# Revit family: Facade smoke exhaust hatch mcr_LAM
name_source: partatom
category: Okna
revit_build: Autodesk Revit 2018 (Build: 20170927_1515(x64)
units: mm (PartAtom-declared; Revit-internal decimal feet)

## family parameters
Obiekt nadrzędny = Powierzchnia
Punkt obliczania pomieszczeń = Nie
Tnij formami wycięć po wczytaniu = Nie
Współdzielony = Nie

## types (199) — shared parameters
Attention = You can choose steel or aluminum for the damper base
DBD = 148 mm
Model = mcr LAM
Opis = "Facade natural smoke and heat exhaust ventilator, louvered type mcr LAM"
Producent = Mercor S.A.
SBD = 150 mm
URL = https://www.mercor.com.pl
mcr_Acces space = mcr_Acces space
mcr_Base = mcr_Aluminium
mcr_Blinds = mcr_Chambered polycarbonate plate
mcr_Family = mcr LAM
mcr_Group = Facade natural smoke and heat exhaust ventilator, louvered type
mcr_Insulation = mcr_Hard mineral wool
mcr_Notes = The weight is given for vent with alu upstand height 15 cm
mcr_Plinth = mcr_Galvanized steel sheet
mcr_Smooth blinds = mcr_Aluminium
mcr_Vent name = Facade natural smoke and heat exhaust ventilator, louvered type mcr LAM
zero-valued in all types: Domyślna rzędna

## per-type parameters (varying)
| type | DZ | OW | mcr_Approximate weight of the device | mcr_CODE | mcr_Nominal dimensions (roof opening dim.) | mcr_Nominal length | mcr_Nominal width | mcr_Number of blades | mcr_Product type |
| LAM 80x50 | 650 mm | 536 mm | 21.50 kg | 800500 | 80x50 cm | 500 mm | 800 mm | 4 | LAM-4-50 |
| LAM 80x60 | 750 mm  [stored 2.46063 ft] | 536 mm | 23.00 kg | 800600 | 80x60 cm | 600 mm | 800 mm | 4 | LAM-4-60 |
| LAM 80x70 | 850 mm | 536 mm | 24.50 kg | 800700 | 80x70 cm | 700 mm | 800 mm | 4 | LAM-4-70 |
| LAM 80x80 | 950 mm | 536 mm | 26.00 kg | 800800 | 80x80 cm | 800 mm | 800 mm | 4 | LAM-4-80 |
| LAM 80x90 | 1050 mm | 536 mm | 27.50 kg | 800900 | 80x90 cm | 900 mm | 800 mm | 4 | LAM-4-90 |
| LAM 80x100 | 1150 mm | 536 mm | 29.00 kg | 8001000 | 80x100 cm | 1000 mm  [stored 3.28084 ft] | 800 mm | 4 | LAM-4-100 |
| LAM 80x110 | 1250 mm  [stored 4.10105 ft] | 536 mm | 30.50 kg | 8001100 | 80x110 cm | 1100 mm  [stored 3.60892 ft] | 800 mm | 4 | LAM-4-110 |
| LAM 80x120 | 1350 mm | 536 mm | 32.00 kg | 8001200 | 80x120 cm | 1200 mm | 800 mm | 4 | LAM-4-120 |
| LAM 80x130 | 1450 mm | 536 mm | 33.50 kg | 8001300 | 80x130 cm | 1300 mm | 800 mm | 4 | LAM-4-130 |
| LAM 80x140 | 1550 mm | 536 mm | 35.00 kg | 8001400 | 80x140 cm | 1400 mm  [stored 4.59318 ft] | 800 mm | 4 | LAM-4-140 |
| LAM 80x150 | 1650 mm | 536 mm | 36.50 kg | 8001500 | 80x150 cm | 1500 mm | 800 mm | 4 | LAM-4-150 |
| LAM 80x160 | 1750 mm | 536 mm | 38.00 kg | 8001600 | 80x160 cm | 1600 mm  [stored 5.24934 ft] | 800 mm | 4 | LAM-4-160 |
| LAM 80x170 | 1850 mm | 536 mm | 39.50 kg | 8001700 | 80x170 cm | 1700 mm | 800 mm | 4 | LAM-4-170 |
| LAM 100x50 | 650 mm | 670 mm | 25.50 kg | 1000500 | 100x50 cm | 500 mm | 1000 mm  [stored 3.28084 ft] | 5 | LAM-5-50 |
| LAM 100x60 | 750 mm  [stored 2.46063 ft] | 670 mm | 27.00 kg | 1000600 | 100x60 cm | 600 mm | 1000 mm  [stored 3.28084 ft] | 5 | LAM-5-60 |
| LAM 100x70 | 850 mm | 670 mm | 28.50 kg | 1000700 | 100x70 cm | 700 mm | 1000 mm  [stored 3.28084 ft] | 5 | LAM-5-70 |
| LAM 100x80 | 950 mm | 670 mm | 30.00 kg | 1000800 | 100x80 cm | 800 mm | 1000 mm  [stored 3.28084 ft] | 5 | LAM-5-80 |
| LAM 100x90 | 1050 mm | 670 mm | 31.50 kg | 1000900 | 100x90 cm | 900 mm | 1000 mm  [stored 3.28084 ft] | 5 | LAM-5-90 |
| LAM 100x100 | 1150 mm | 670 mm | 33.00 kg | 10001000 | 100x100 cm | 1000 mm  [stored 3.28084 ft] | 1000 mm  [stored 3.28084 ft] | 5 | LAM-5-100 |
| LAM 100x110 | 1250 mm  [stored 4.10105 ft] | 670 mm | 34.50 kg | 10001100 | 100x110 cm | 1100 mm  [stored 3.60892 ft] | 1000 mm  [stored 3.28084 ft] | 5 | LAM-5-110 |
| LAM 100x120 | 1350 mm | 670 mm | 36.00 kg | 10001200 | 100x120 cm | 1200 mm | 1000 mm  [stored 3.28084 ft] | 5 | LAM-5-120 |
| LAM 100x130 | 1450 mm | 670 mm | 37.50 kg | 10001300 | 100x130 cm | 1300 mm | 1000 mm  [stored 3.28084 ft] | 5 | LAM-5-130 |
| LAM 100x140 | 1550 mm | 670 mm | 39.00 kg | 10001400 | 100x140 cm | 1400 mm  [stored 4.59318 ft] | 1000 mm  [stored 3.28084 ft] | 5 | LAM-5-140 |
| LAM 100x150 | 1650 mm | 670 mm | 40.50 kg | 10001500 | 100x150 cm | 1500 mm | 1000 mm  [stored 3.28084 ft] | 5 | LAM-5-150 |
| LAM 100x160 | 1750 mm | 670 mm | 42.00 kg | 10001600 | 100x160 cm | 1600 mm  [stored 5.24934 ft] | 1000 mm  [stored 3.28084 ft] | 5 | LAM-5-160 |
| LAM 100x170 | 1850 mm | 670 mm | 43.50 kg | 10001700 | 100x170 cm | 1700 mm | 1000 mm  [stored 3.28084 ft] | 5 | LAM-5-170 |
| LAM 100x180 | 1950 mm | 670 mm | 45.00 kg | 10001800 | 100x180 cm | 1800 mm | 1000 mm  [stored 3.28084 ft] | 5 | LAM-5-180 |
| LAM 100x190 | 2050 mm | 670 mm | 46.50 kg | 10001900 | 100x190 cm | 1900 mm | 1000 mm  [stored 3.28084 ft] | 5 | LAM-5-190 |
| LAM 100x200 | 2150 mm | 670 mm | 48.00 kg | 10002000 | 100x200 cm | 2000 mm | 1000 mm  [stored 3.28084 ft] | 5 | LAM-5-200 |
| LAM 100x210 | 2250 mm | 670 mm | 49.50 kg | 10002100 | 100x210 cm | 2100 mm | 1000 mm  [stored 3.28084 ft] | 5 | LAM-5-210 |
| LAM 120x50 | 650 mm | 804 mm | 29.50 kg | 1200500 | 120x50 cm | 500 mm | 1200 mm | 6 | LAM-6-50 |
| LAM 120x60 | 750 mm  [stored 2.46063 ft] | 804 mm | 31.00 kg | 1200600 | 120x60 cm | 600 mm | 1200 mm | 6 | LAM-6-60 |
| LAM 120x70 | 850 mm | 804 mm | 32.50 kg | 1200700 | 120x70 cm | 700 mm | 1200 mm | 6 | LAM-6-70 |
| LAM 120x80 | 950 mm | 804 mm | 34.00 kg | 1200800 | 120x80 cm | 800 mm | 1200 mm | 6 | LAM-6-80 |
| LAM 120x90 | 1050 mm | 804 mm | 35.50 kg | 1200900 | 120x90 cm | 900 mm | 1200 mm | 6 | LAM-6-90 |
| LAM 120x100 | 1150 mm | 804 mm | 37.00 kg | 12001000 | 120x100 cm | 1000 mm  [stored 3.28084 ft] | 1200 mm | 6 | LAM-6-100 |
| LAM 120x110 | 1250 mm  [stored 4.10105 ft] | 804 mm | 38.75 kg | 12001100 | 120x110 cm | 1100 mm  [stored 3.60892 ft] | 1200 mm | 6 | LAM-6-110 |
| LAM 120x120 | 1350 mm | 804 mm | 40.50 kg | 12001200 | 120x120 cm | 1200 mm | 1200 mm | 6 | LAM-6-120 |
| LAM 120x130 | 1450 mm | 804 mm | 42.25 kg | 12001300 | 120x130 cm | 1300 mm | 1200 mm | 6 | LAM-6-130 |
| LAM 120x140 | 1550 mm | 804 mm | 44.00 kg | 12001400 | 120x140 cm | 1400 mm  [stored 4.59318 ft] | 1200 mm | 6 | LAM-6-140 |
| LAM 120x150 | 1650 mm | 804 mm | 45.75 kg | 12001500 | 120x150 cm | 1500 mm | 1200 mm | 6 | LAM-6-150 |
| LAM 120x160 | 1750 mm | 804 mm | 47.50 kg | 12001600 | 120x160 cm | 1600 mm  [stored 5.24934 ft] | 1200 mm | 6 | LAM-6-160 |
| LAM 120x170 | 1850 mm | 804 mm | 49.25 kg | 12001700 | 120x170 cm | 1700 mm | 1200 mm | 6 | LAM-6-170 |
| LAM 120x180 | 1950 mm | 804 mm | 51.00 kg | 12001800 | 120x180 cm | 1800 mm | 1200 mm | 6 | LAM-6-180 |
| LAM 120x190 | 2050 mm | 804 mm | 52.75 kg | 12001900 | 120x190 cm | 1900 mm | 1200 mm | 6 | LAM-6-190 |
| LAM 120x200 | 2150 mm | 804 mm | 54.50 kg | 12002000 | 120x200 cm | 2000 mm | 1200 mm | 6 | LAM-6-200 |
| LAM 120x210 | 2250 mm | 804 mm | 56.25 kg | 12002100 | 120x210 cm | 2100 mm | 1200 mm | 6 | LAM-6-210 |
| LAM 120x220 | 2350 mm | 804 mm | 58.00 kg | 12002200 | 120x220 cm | 2200 mm | 1200 mm | 6 | LAM-6-220 |
| LAM 120x230 | 2450 mm | 804 mm | 59.75 kg | 12002300 | 120x230 cm | 2300 mm | 1200 mm | 6 | LAM-6-230 |
| LAM 120x240 | 2550 mm | 804 mm | 61.50 kg | 12002400 | 120x240 cm | 2400 mm | 1200 mm | 6 | LAM-6-240 |
| LAM 120x250 | 2650 mm | 804 mm | 65.00 kg | 12002500 | 120x250 cm | 2500 mm | 1200 mm | 6 | LAM-6-250 |
| LAM 140x60 | 750 mm  [stored 2.46063 ft] | 938 mm | 31.00 kg | 1400600 | 140x60 cm | 600 mm | 1400 mm  [stored 4.59318 ft] | 7 | LAM-7-60 |
| LAM 140x70 | 850 mm | 938 mm | 33.50 kg | 1400700 | 140x70 cm | 700 mm | 1400 mm  [stored 4.59318 ft] | 7 | LAM-7-70 |
| LAM 140x80 | 950 mm | 938 mm | 36.00 kg | 1400800 | 140x80 cm | 800 mm | 1400 mm  [stored 4.59318 ft] | 7 | LAM-7-80 |
| LAM 140x90 | 1050 mm | 938 mm | 38.50 kg | 1400900 | 140x90 cm | 900 mm | 1400 mm  [stored 4.59318 ft] | 7 | LAM-7-90 |
| LAM 140x100 | 1150 mm | 938 mm | 41.00 kg | 14001000 | 140x100 cm | 1000 mm  [stored 3.28084 ft] | 1400 mm  [stored 4.59318 ft] | 7 | LAM-7-100 |
| LAM 140x110 | 1250 mm  [stored 4.10105 ft] | 938 mm | 43.50 kg | 14001100 | 140x110 cm | 1100 mm  [stored 3.60892 ft] | 1400 mm  [stored 4.59318 ft] | 7 | LAM-7-110 |
| LAM 140x120 | 1350 mm | 938 mm | 45.50 kg | 14001200 | 140x120 cm | 1200 mm | 1400 mm  [stored 4.59318 ft] | 7 | LAM-7-120 |
| LAM 140x130 | 1450 mm | 938 mm | 48.00 kg | 14001300 | 140x130 cm | 1300 mm | 1400 mm  [stored 4.59318 ft] | 7 | LAM-7-130 |
| LAM 140x140 | 1550 mm | 938 mm | 49.00 kg | 14001400 | 140x140 cm | 1400 mm  [stored 4.59318 ft] | 1400 mm  [stored 4.59318 ft] | 7 | LAM-7-140 |
| LAM 140x150 | 1650 mm | 938 mm | 51.50 kg | 14001500 | 140x150 cm | 1500 mm | 1400 mm  [stored 4.59318 ft] | 7 | LAM-7-150 |
| LAM 140x160 | 1750 mm | 938 mm | 52.50 kg | 14001600 | 140x160 cm | 1600 mm  [stored 5.24934 ft] | 1400 mm  [stored 4.59318 ft] | 7 | LAM-7-160 |
| LAM 140x170 | 1850 mm | 938 mm | 55.00 kg | 14001700 | 140x170 cm | 1700 mm | 1400 mm  [stored 4.59318 ft] | 7 | LAM-7-170 |
| LAM 140x180 | 1950 mm | 938 mm | 56.00 kg | 14001800 | 140x180 cm | 1800 mm | 1400 mm  [stored 4.59318 ft] | 7 | LAM-7-180 |
| LAM 140x190 | 2050 mm | 938 mm | 58.50 kg | 14001900 | 140x190 cm | 1900 mm | 1400 mm  [stored 4.59318 ft] | 7 | LAM-7-190 |
| LAM 140x200 | 2150 mm | 938 mm | 59.50 kg | 14002000 | 140x200 cm | 2000 mm | 1400 mm  [stored 4.59318 ft] | 7 | LAM-7-200 |
| LAM 140x210 | 2250 mm | 938 mm | 62.00 kg | 14002100 | 140x210 cm | 2100 mm | 1400 mm  [stored 4.59318 ft] | 7 | LAM-7-210 |
| LAM 140x220 | 2350 mm | 938 mm | 63.00 kg | 14002200 | 140x220 cm | 2200 mm | 1400 mm  [stored 4.59318 ft] | 7 | LAM-7-220 |
| LAM 140x230 | 2450 mm | 938 mm | 65.50 kg | 14002300 | 140x230 cm | 2300 mm | 1400 mm  [stored 4.59318 ft] | 7 | LAM-7-230 |
| LAM 140x240 | 2550 mm | 938 mm | 66.50 kg | 14002400 | 140x240 cm | 2400 mm | 1400 mm  [stored 4.59318 ft] | 7 | LAM-7-240 |
| LAM 140x250 | 2650 mm | 938 mm | 70.00 kg | 14002500 | 140x250 cm | 2500 mm | 1400 mm  [stored 4.59318 ft] | 7 | LAM-7-250 |
| LAM 160x70 | 850 mm | 1072 mm | 36.75 kg | 1600700 | 160x70 cm | 700 mm | 1600 mm  [stored 5.24934 ft] | 8 | LAM-8-70 |
| LAM 160x80 | 950 mm | 1072 mm | 39.50 kg | 1600800 | 160x80 cm | 800 mm | 1600 mm  [stored 5.24934 ft] | 8 | LAM-8-80 |
| LAM 160x90 | 1050 mm | 1072 mm | 42.25 kg | 1600900 | 160x90 cm | 900 mm | 1600 mm  [stored 5.24934 ft] | 8 | LAM-8-90 |
| LAM 160x100 | 1150 mm | 1072 mm | 45.00 kg | 16001000 | 160x100 cm | 1000 mm  [stored 3.28084 ft] | 1600 mm  [stored 5.24934 ft] | 8 | LAM-8-100 |
| LAM 160x110 | 1250 mm  [stored 4.10105 ft] | 1072 mm | 47.75 kg | 16001100 | 160x110 cm | 1100 mm  [stored 3.60892 ft] | 1600 mm  [stored 5.24934 ft] | 8 | LAM-8-110 |
| LAM 160x120 | 1350 mm | 1072 mm | 50.50 kg | 16001200 | 160x120 cm | 1200 mm | 1600 mm  [stored 5.24934 ft] | 8 | LAM-8-120 |
| LAM 160x130 | 1450 mm | 1072 mm | 53.25 kg | 16001300 | 160x130 cm | 1300 mm | 1600 mm  [stored 5.24934 ft] | 8 | LAM-8-130 |
| LAM 160x140 | 1550 mm | 1072 mm | 56.00 kg | 16001400 | 160x140 cm | 1400 mm  [stored 4.59318 ft] | 1600 mm  [stored 5.24934 ft] | 8 | LAM-8-140 |
| LAM 160x150 | 1650 mm | 1072 mm | 58.75 kg | 16001500 | 160x150 cm | 1500 mm | 1600 mm  [stored 5.24934 ft] | 8 | LAM-8-150 |
| LAM 160x160 | 1750 mm | 1072 mm | 61.50 kg | 16001600 | 160x160 cm | 1600 mm  [stored 5.24934 ft] | 1600 mm  [stored 5.24934 ft] | 8 | LAM-8-160 |
| LAM 160x170 | 1850 mm | 1072 mm | 64.25 kg | 16001700 | 160x170 cm | 1700 mm | 1600 mm  [stored 5.24934 ft] | 8 | LAM-8-170 |
| LAM 160x180 | 1950 mm | 1072 mm | 67.00 kg | 16001800 | 160x180 cm | 1800 mm | 1600 mm  [stored 5.24934 ft] | 8 | LAM-8-180 |
| LAM 160x190 | 2050 mm | 1072 mm | 69.75 kg | 16001900 | 160x190 cm | 1900 mm | 1600 mm  [stored 5.24934 ft] | 8 | LAM-8-190 |
| LAM 160x200 | 2150 mm | 1072 mm | 72.50 kg | 16002000 | 160x200 cm | 2000 mm | 1600 mm  [stored 5.24934 ft] | 8 | LAM-8-200 |
| LAM 160x210 | 2250 mm | 1072 mm | 75.25 kg | 16002100 | 160x210 cm | 2100 mm | 1600 mm  [stored 5.24934 ft] | 8 | LAM-8-210 |
| LAM 160x220 | 2350 mm | 1072 mm | 78.00 kg | 16002200 | 160x220 cm | 2200 mm | 1600 mm  [stored 5.24934 ft] | 8 | LAM-8-220 |
| LAM 160x230 | 2450 mm | 1072 mm | 80.75 kg | 16002300 | 160x230 cm | 2300 mm | 1600 mm  [stored 5.24934 ft] | 8 | LAM-8-230 |
| LAM 160x240 | 2550 mm | 1072 mm | 83.50 kg | 16002400 | 160x240 cm | 2400 mm | 1600 mm  [stored 5.24934 ft] | 8 | LAM-8-240 |
| LAM 160x250 | 2650 mm | 1072 mm | 89.00 kg | 16002500 | 160x250 cm | 2500 mm | 1600 mm  [stored 5.24934 ft] | 8 | LAM-8-250 |
| LAM 180x80 | 950 mm | 1206 mm | 43.00 kg | 1800800 | 180x80 cm | 800 mm | 1800 mm | 9 | LAM-9-80 |
| LAM 180x90 | 1050 mm | 1206 mm | 46.00 kg | 1800900 | 180x90 cm | 900 mm | 1800 mm | 9 | LAM-9-90 |
| LAM 180x100 | 1150 mm | 1206 mm | 49.00 kg | 18001000 | 180x100 cm | 1000 mm  [stored 3.28084 ft] | 1800 mm | 9 | LAM-9-100 |
| LAM 180x110 | 1250 mm  [stored 4.10105 ft] | 1206 mm | 52.00 kg | 18001100 | 180x110 cm | 1100 mm  [stored 3.60892 ft] | 1800 mm | 9 | LAM-9-110 |
| LAM 180x120 | 1350 mm | 1206 mm | 55.00 kg | 18001200 | 180x120 cm | 1200 mm | 1800 mm | 9 | LAM-9-120 |
| LAM 180x130 | 1450 mm | 1206 mm | 58.00 kg | 18001300 | 180x130 cm | 1300 mm | 1800 mm | 9 | LAM-9-130 |
| LAM 180x140 | 1550 mm | 1206 mm | 61.00 kg | 18001400 | 180x140 cm | 1400 mm  [stored 4.59318 ft] | 1800 mm | 9 | LAM-9-140 |
| LAM 180x150 | 1650 mm | 1206 mm | 64.00 kg | 18001500 | 180x150 cm | 1500 mm | 1800 mm | 9 | LAM-9-150 |
| LAM 180x160 | 1750 mm | 1206 mm | 67.00 kg | 18001600 | 180x160 cm | 1600 mm  [stored 5.24934 ft] | 1800 mm | 9 | LAM-9-160 |
| LAM 180x170 | 1850 mm | 1206 mm | 70.00 kg | 18001700 | 180x170 cm | 1700 mm | 1800 mm | 9 | LAM-9-170 |
| LAM 180x180 | 1950 mm | 1206 mm | 73.00 kg | 18001800 | 180x180 cm | 1800 mm | 1800 mm | 9 | LAM-9-180 |
| LAM 180x190 | 2050 mm | 1206 mm | 76.00 kg | 18001900 | 180x190 cm | 1900 mm | 1800 mm | 9 | LAM-9-190 |
| LAM 180x200 | 2150 mm | 1206 mm | 79.00 kg | 18002000 | 180x200 cm | 2000 mm | 1800 mm | 9 | LAM-9-200 |
| LAM 180x210 | 2250 mm | 1206 mm | 82.00 kg | 18002100 | 180x210 cm | 2100 mm | 1800 mm | 9 | LAM-9-210 |
| LAM 180x220 | 2350 mm | 1206 mm | 85.00 kg | 18002200 | 180x220 cm | 2200 mm | 1800 mm | 9 | LAM-9-220 |
| LAM 180x230 | 2450 mm | 1206 mm | 88.00 kg | 18002300 | 180x230 cm | 2300 mm | 1800 mm | 9 | LAM-9-230 |
| LAM 180x240 | 2550 mm | 1206 mm | 91.00 kg | 18002400 | 180x240 cm | 2400 mm | 1800 mm | 9 | LAM-9-240 |
| LAM 180x250 | 2650 mm | 1206 mm | 97.00 kg | 18002500 | 180x250 cm | 2500 mm | 1800 mm | 9 | LAM-9-250 |
| LAM 200x90 | 1050 mm | 1340 mm | 49.75 kg | 2000900 | 200x90 cm | 900 mm | 2000 mm | 10 | LAM-10-90 |
| LAM 200x100 | 1150 mm | 1340 mm | 53.00 kg | 20001000 | 200x100 cm | 1000 mm  [stored 3.28084 ft] | 2000 mm | 10 | LAM-10-100 |
| LAM 200x110 | 1250 mm  [stored 4.10105 ft] | 1340 mm | 56.25 kg | 20001100 | 200x110 cm | 1100 mm  [stored 3.60892 ft] | 2000 mm | 10 | LAM-10-110 |
| LAM 200x120 | 1350 mm | 1340 mm | 59.50 kg | 20001200 | 200x120 cm | 1200 mm | 2000 mm | 10 | LAM-10-120 |
| LAM 200x130 | 1450 mm | 1340 mm | 62.75 kg | 20001300 | 200x130 cm | 1300 mm | 2000 mm | 10 | LAM-10-130 |
| LAM 200x140 | 1550 mm | 1340 mm | 66.00 kg | 20001400 | 200x140 cm | 1400 mm  [stored 4.59318 ft] | 2000 mm | 10 | LAM-10-140 |
| LAM 200x150 | 1650 mm | 1340 mm | 69.25 kg | 20001500 | 200x150 cm | 1500 mm | 2000 mm | 10 | LAM-10-150 |
| LAM 200x160 | 1750 mm | 1340 mm | 72.50 kg | 20001600 | 200x160 cm | 1600 mm  [stored 5.24934 ft] | 2000 mm | 10 | LAM-10-160 |
| LAM 200x170 | 1850 mm | 1340 mm | 75.75 kg | 20001700 | 200x170 cm | 1700 mm | 2000 mm | 10 | LAM-10-170 |
| LAM 200x180 | 1950 mm | 1340 mm | 79.00 kg | 20001800 | 200x180 cm | 1800 mm | 2000 mm | 10 | LAM-10-180 |
| LAM 200x190 | 2050 mm | 1340 mm | 82.25 kg | 20001900 | 200x190 cm | 1900 mm | 2000 mm | 10 | LAM-10-190 |
| LAM 200x200 | 2150 mm | 1340 mm | 85.50 kg | 20002000 | 200x200 cm | 2000 mm | 2000 mm | 10 | LAM-10-200 |
| LAM 200x210 | 2250 mm | 1340 mm | 88.75 kg | 20002100 | 200x210 cm | 2100 mm | 2000 mm | 10 | LAM-10-210 |
| LAM 200x220 | 2350 mm | 1340 mm | 92.00 kg | 20002200 | 200x220 cm | 2200 mm | 2000 mm | 10 | LAM-10-220 |
| LAM 200x230 | 2450 mm | 1340 mm | 95.25 kg | 20002300 | 200x230 cm | 2300 mm | 2000 mm | 10 | LAM-10-230 |
| LAM 200x240 | 2550 mm | 1340 mm | 98.50 kg | 20002400 | 200x240 cm | 2400 mm | 2000 mm | 10 | LAM-10-240 |
| LAM 200x250 | 2650 mm | 1340 mm | 105.00 kg | 20002500 | 200x250 cm | 2500 mm | 2000 mm | 10 | LAM-10-250 |
| LAM 220x100 | 1150 mm | 1474 mm | 57.00 kg | 22001000 | 220x100 cm | 1000 mm  [stored 3.28084 ft] | 2200 mm | 11 | LAM-11-100 |
| LAM 220x110 | 1250 mm  [stored 4.10105 ft] | 1474 mm | 67.50 kg | 22001100 | 220x110 cm | 1100 mm  [stored 3.60892 ft] | 2200 mm | 11 | LAM-11-110 |
| LAM 220x120 | 1350 mm | 1474 mm | 64.00 kg | 22001200 | 220x120 cm | 1200 mm | 2200 mm | 11 | LAM-11-120 |
| LAM 220x130 | 1450 mm | 1474 mm | 74.50 kg | 22001300 | 220x130 cm | 1300 mm | 2200 mm | 11 | LAM-11-130 |
| LAM 220x140 | 1550 mm | 1474 mm | 71.00 kg | 22001400 | 220x140 cm | 1400 mm  [stored 4.59318 ft] | 2200 mm | 11 | LAM-11-140 |
| LAM 220x150 | 1650 mm | 1474 mm | 81.50 kg | 22001500 | 220x150 cm | 1500 mm | 2200 mm | 11 | LAM-11-150 |
| LAM 220x160 | 1750 mm | 1474 mm | 78.00 kg | 22001600 | 220x160 cm | 1600 mm  [stored 5.24934 ft] | 2200 mm | 11 | LAM-11-160 |
| LAM 220x170 | 1850 mm | 1474 mm | 88.50 kg | 22001700 | 220x170 cm | 1700 mm | 2200 mm | 11 | LAM-11-170 |
| LAM 220x180 | 1950 mm | 1474 mm | 85.00 kg | 22001800 | 220x180 cm | 1800 mm | 2200 mm | 11 | LAM-11-180 |
| LAM 220x190 | 2050 mm | 1474 mm | 95.50 kg | 22001900 | 220x190 cm | 1900 mm | 2200 mm | 11 | LAM-11-190 |
| LAM 220x200 | 2150 mm | 1474 mm | 92.00 kg | 22002000 | 220x200 cm | 2000 mm | 2200 mm | 11 | LAM-11-200 |
| LAM 220x210 | 2250 mm | 1474 mm | 102.50 kg | 22002100 | 220x210 cm | 2100 mm | 2200 mm | 11 | LAM-11-210 |
| LAM 220x220 | 2350 mm | 1474 mm | 99.00 kg | 22002200 | 220x220 cm | 2200 mm | 2200 mm | 11 | LAM-11-220 |
| LAM 220x230 | 2450 mm | 1474 mm | 109.50 kg | 22002300 | 220x230 cm | 2300 mm | 2200 mm | 11 | LAM-11-230 |
| LAM 220x240 | 2550 mm | 1474 mm | 106.00 kg | 22002400 | 220x240 cm | 2400 mm | 2200 mm | 11 | LAM-11-240 |
| LAM 220x250 | 2650 mm | 1474 mm | 113.00 kg | 22002500 | 220x250 cm | 2500 mm | 2200 mm | 11 | LAM-11-250 |
| LAM 240x100 | 1150 mm | 1608 mm | 61.00 kg | 24001000 | 240x100 cm | 1000 mm  [stored 3.28084 ft] | 2400 mm | 12 | LAM-12-100 |
| LAM 240x110 | 1250 mm  [stored 4.10105 ft] | 1608 mm | 64.75 kg | 24001100 | 240x110 cm | 1100 mm  [stored 3.60892 ft] | 2400 mm | 12 | LAM-12-110 |
| LAM 240x120 | 1350 mm | 1608 mm | 68.50 kg | 24001200 | 240x120 cm | 1200 mm | 2400 mm | 12 | LAM-12-120 |
| LAM 240x130 | 1450 mm | 1608 mm | 72.25 kg | 24001300 | 240x130 cm | 1300 mm | 2400 mm | 12 | LAM-12-130 |
| LAM 240x140 | 1550 mm | 1608 mm | 76.00 kg | 24001400 | 240x140 cm | 1400 mm  [stored 4.59318 ft] | 2400 mm | 12 | LAM-12-140 |
| LAM 240x150 | 1650 mm | 1608 mm | 79.75 kg | 24001500 | 240x150 cm | 1500 mm | 2400 mm | 12 | LAM-12-150 |
| LAM 240x160 | 1750 mm | 1608 mm | 83.50 kg | 24001600 | 240x160 cm | 1600 mm  [stored 5.24934 ft] | 2400 mm | 12 | LAM-12-160 |
| LAM 240x170 | 1850 mm | 1608 mm | 87.25 kg | 24001700 | 240x170 cm | 1700 mm | 2400 mm | 12 | LAM-12-170 |
| LAM 240x180 | 1950 mm | 1608 mm | 91.00 kg | 24001800 | 240x180 cm | 1800 mm | 2400 mm | 12 | LAM-12-180 |
| LAM 240x190 | 2050 mm | 1608 mm | 94.75 kg | 24001900 | 240x190 cm | 1900 mm | 2400 mm | 12 | LAM-12-190 |
| LAM 240x200 | 2150 mm | 1608 mm | 98.50 kg | 24002000 | 240x200 cm | 2000 mm | 2400 mm | 12 | LAM-12-200 |
| LAM 240x210 | 2250 mm | 1608 mm | 102.25 kg | 24002100 | 240x210 cm | 2100 mm | 2400 mm | 12 | LAM-12-210 |
| LAM 240x220 | 2350 mm | 1608 mm | 106.00 kg | 24002200 | 240x220 cm | 2200 mm | 2400 mm | 12 | LAM-12-220 |
| LAM 240x230 | 2450 mm | 1608 mm | 109.75 kg | 24002300 | 240x230 cm | 2300 mm | 2400 mm | 12 | LAM-12-230 |
| LAM 240x240 | 2550 mm | 1608 mm | 113.50 kg | 24002400 | 240x240 cm | 2400 mm | 2400 mm | 12 | LAM-12-240 |
| LAM 240x250 | 2650 mm | 1608 mm | 121.00 kg | 24002500 | 240x250 cm | 2500 mm | 2400 mm | 12 | LAM-12-250 |
| LAM 260x110 | 1250 mm  [stored 4.10105 ft] | 1742 mm | 69.00 kg | 26001100 | 260x110 cm | 1100 mm  [stored 3.60892 ft] | 2600 mm | 13 | LAM-13-110 |
| LAM 260x120 | 1350 mm | 1742 mm | 73.00 kg | 26001200 | 260x120 cm | 1200 mm | 2600 mm | 13 | LAM-13-120 |
| LAM 260x130 | 1450 mm | 1742 mm | 77.00 kg | 26001300 | 260x130 cm | 1300 mm | 2600 mm | 13 | LAM-13-130 |
| LAM 260x140 | 1550 mm | 1742 mm | 81.00 kg | 26001400 | 260x140 cm | 1400 mm  [stored 4.59318 ft] | 2600 mm | 13 | LAM-13-140 |
| LAM 260x150 | 1650 mm | 1742 mm | 85.00 kg | 26001500 | 260x150 cm | 1500 mm | 2600 mm | 13 | LAM-13-150 |
| LAM 260x160 | 1750 mm | 1742 mm | 89.00 kg | 26001600 | 260x160 cm | 1600 mm  [stored 5.24934 ft] | 2600 mm | 13 | LAM-13-160 |
| LAM 260x170 | 1850 mm | 1742 mm | 93.00 kg | 26001700 | 260x170 cm | 1700 mm | 2600 mm | 13 | LAM-13-170 |
| LAM 260x180 | 1950 mm | 1742 mm | 97.00 kg | 26001800 | 260x180 cm | 1800 mm | 2600 mm | 13 | LAM-13-180 |
| LAM 260x190 | 2050 mm | 1742 mm | 101.00 kg | 26001900 | 260x190 cm | 1900 mm | 2600 mm | 13 | LAM-13-190 |
| LAM 260x200 | 2150 mm | 1742 mm | 105.00 kg | 26002000 | 260x200 cm | 2000 mm | 2600 mm | 13 | LAM-13-200 |
| LAM 260x210 | 2250 mm | 1742 mm | 109.00 kg | 26002100 | 260x210 cm | 2100 mm | 2600 mm | 13 | LAM-13-210 |
| LAM 260x220 | 2350 mm | 1742 mm | 113.00 kg | 26002200 | 260x220 cm | 2200 mm | 2600 mm | 13 | LAM-13-220 |
| LAM 260x230 | 2450 mm | 1742 mm | 117.00 kg | 26002300 | 260x230 cm | 2300 mm | 2600 mm | 13 | LAM-13-230 |
| LAM 260x240 | 2550 mm | 1742 mm | 121.00 kg | 26002400 | 260x240 cm | 2400 mm | 2600 mm | 13 | LAM-13-240 |
| LAM 260x250 | 2650 mm | 1742 mm | 129.00 kg | 26002500 | 260x250 cm | 2500 mm | 2600 mm | 13 | LAM-13-250 |
| LAM 280x120 | 1350 mm | 1876 mm | 77.50 kg | 28001200 | 280x120 cm | 1200 mm | 2800 mm | 14 | LAM-14-120 |
| LAM 280x130 | 1450 mm | 1876 mm | 81.75 kg | 28001300 | 280x130 cm | 1300 mm | 2800 mm | 14 | LAM-14-130 |
| LAM 280x140 | 1550 mm | 1876 mm | 86.00 kg | 28001400 | 280x140 cm | 1400 mm  [stored 4.59318 ft] | 2800 mm | 14 | LAM-14-140 |
| LAM 280x150 | 1650 mm | 1876 mm | 90.25 kg | 28001500 | 280x150 cm | 1500 mm | 2800 mm | 14 | LAM-14-150 |
| LAM 280x160 | 1750 mm | 1876 mm | 94.50 kg | 28001600 | 280x160 cm | 1600 mm  [stored 5.24934 ft] | 2800 mm | 14 | LAM-14-160 |
| LAM 280x170 | 1850 mm | 1876 mm | 98.75 kg | 28001700 | 280x170 cm | 1700 mm | 2800 mm | 14 | LAM-14-170 |
| LAM 280x180 | 1950 mm | 1876 mm | 103.00 kg | 28001800 | 280x180 cm | 1800 mm | 2800 mm | 14 | LAM-14-180 |
| LAM 280x190 | 2050 mm | 1876 mm | 107.25 kg | 28001900 | 280x190 cm | 1900 mm | 2800 mm | 14 | LAM-14-190 |
| LAM 280x200 | 2150 mm | 1876 mm | 111.50 kg | 28002000 | 280x200 cm | 2000 mm | 2800 mm | 14 | LAM-14-200 |
| LAM 280x210 | 2250 mm | 1876 mm | 115.75 kg | 28002100 | 280x210 cm | 2100 mm | 2800 mm | 14 | LAM-14-210 |
| LAM 280x220 | 2350 mm | 1876 mm | 120.00 kg | 28002200 | 280x220 cm | 2200 mm | 2800 mm | 14 | LAM-14-220 |
| LAM 280x230 | 2450 mm | 1876 mm | 124.25 kg | 28002300 | 280x230 cm | 2300 mm | 2800 mm | 14 | LAM-14-230 |
| LAM 280x240 | 2550 mm | 1876 mm | 128.50 kg | 28002400 | 280x240 cm | 2400 mm | 2800 mm | 14 | LAM-14-240 |
| LAM 280x250 | 2650 mm | 1876 mm | 137.00 kg | 28002500 | 280x250 cm | 2500 mm | 2800 mm | 14 | LAM-14-250 |
| LAM 300x130 | 1450 mm | 2010 mm | 86.50 kg | 30001300 | 300x130 cm | 1300 mm | 3000 mm | 15 | LAM-15-130 |
| LAM 300x140 | 1550 mm | 2010 mm | 91.00 kg | 30001400 | 300x140 cm | 1400 mm  [stored 4.59318 ft] | 3000 mm | 15 | LAM-15-140 |
| LAM 300x150 | 1650 mm | 2010 mm | 95.50 kg | 30001500 | 300x150 cm | 1500 mm | 3000 mm | 15 | LAM-15-150 |
| LAM 300x160 | 1750 mm | 2010 mm | 100.00 kg | 30001600 | 300x160 cm | 1600 mm  [stored 5.24934 ft] | 3000 mm | 15 | LAM-15-160 |
| LAM 300x170 | 1850 mm | 2010 mm | 104.50 kg | 30001700 | 300x170 cm | 1700 mm | 3000 mm | 15 | LAM-15-170 |
| LAM 300x180 | 1950 mm | 2010 mm | 109.00 kg | 30001800 | 300x180 cm | 1800 mm | 3000 mm | 15 | LAM-15-180 |
| LAM 300x190 | 2050 mm | 2010 mm | 113.50 kg | 30001900 | 300x190 cm | 1900 mm | 3000 mm | 15 | LAM-15-190 |
| LAM 300x200 | 2150 mm | 2010 mm | 118.00 kg | 30002000 | 300x200 cm | 2000 mm | 3000 mm | 15 | LAM-15-200 |
| LAM 300x210 | 2250 mm | 2010 mm | 122.50 kg | 30002100 | 300x210 cm | 2100 mm | 3000 mm | 15 | LAM-15-210 |
| LAM 300x220 | 2350 mm | 2010 mm | 127.00 kg | 30002200 | 300x220 cm | 2200 mm | 3000 mm | 15 | LAM-15-220 |
| LAM 300x230 | 2450 mm | 2010 mm | 131.50 kg | 30002300 | 300x230 cm | 2300 mm | 3000 mm | 15 | LAM-15-230 |
| LAM 300x240 | 2550 mm | 2010 mm | 136.00 kg | 30002400 | 300x240 cm | 2400 mm | 3000 mm | 15 | LAM-15-240 |
| LAM 300x250 | 2650 mm | 2010 mm | 145.00 kg | 30002500 | 300x250 cm | 2500 mm | 3000 mm | 15 | LAM-15-250 |

note: [stored X ft] marks values corroborated as IEEE doubles in the binary element streams (Revit-internal decimal feet)

## geometry (parser evidence)
native form markers: Sweep x5
no freeform markers — native parametric forms only
